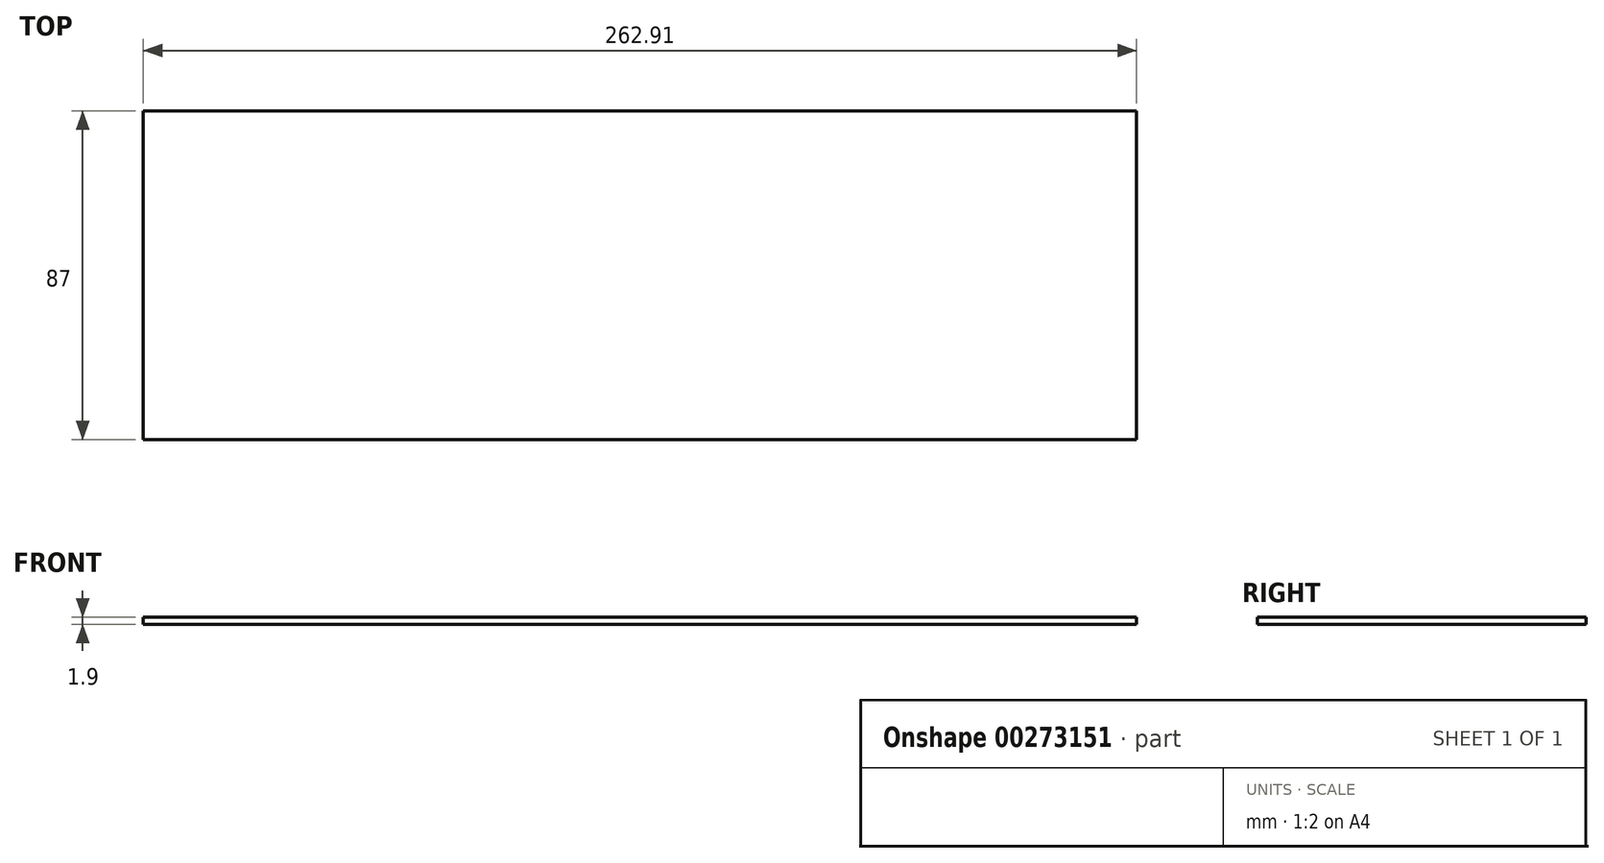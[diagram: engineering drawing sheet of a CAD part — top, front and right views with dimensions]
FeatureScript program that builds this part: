
annotation { "Feature Type Name" : "Feature", "Feature Type Description" : "" }
export const myFeature = defineFeature(function(context is Context, id is Id, definition is map)
    precondition{}
    {
        {
            var Q0;
            Q0=qCreatedBy(makeId("Top.planeOp"),FACE);
            var sketch = newSketch(context, id + "F0", { "sketchPlane" : qUnion([Q0])});
            skLineSegment(sketch, "E0.bottom", {"start": v(0, 0) * mm, "end": v(262.9, 0) * mm});
            skLineSegment(sketch, "E0.top", {"start": v(0, -87) * mm, "end": v(262.9, -87) * mm});
            skLineSegment(sketch, "E0.left", {"start": v(0, 0) * mm, "end": v(0, -87) * mm});
            skLineSegment(sketch, "E0.right", {"start": v(262.9, 0) * mm, "end": v(262.9, -87) * mm});
            skSolve(sketch);
        }
        {
            var Q0;
            Q0 = qSketchRegion(id + "F0", true);
            extrude(context, id + "F1", {"entities" : qUnion([Q0]), "depth" : 1.9 * mm});
        }
    });
